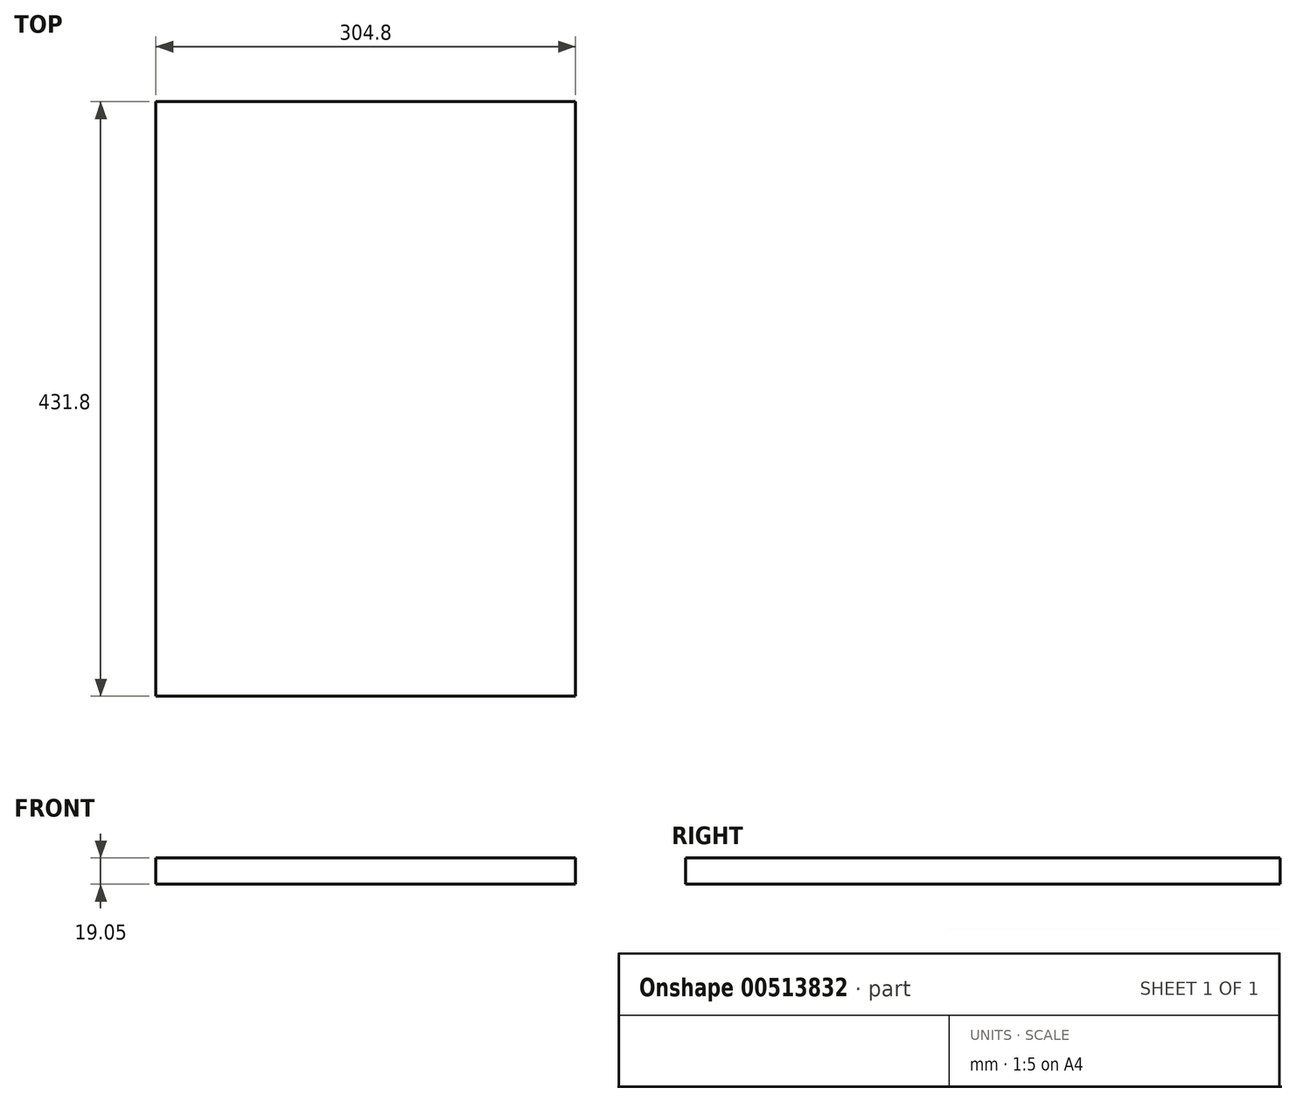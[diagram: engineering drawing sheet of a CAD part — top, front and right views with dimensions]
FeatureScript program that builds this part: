
annotation { "Feature Type Name" : "Feature", "Feature Type Description" : "" }
export const myFeature = defineFeature(function(context is Context, id is Id, definition is map)
    precondition{}
    {
        {
            var Q0;
            Q0=qCreatedBy(makeId("Top.planeOp"),FACE);
            var sketch = newSketch(context, id + "F0", { "sketchPlane" : qUnion([Q0])});
            skLineSegment(sketch, "E0.bottom", {"start": v(152.4, 215.9) * mm, "end": v(-152.4, 215.9) * mm});
            skLineSegment(sketch, "E0.top", {"start": v(152.4, -215.9) * mm, "end": v(-152.4, -215.9) * mm});
            skLineSegment(sketch, "E0.left", {"start": v(152.4, 215.9) * mm, "end": v(152.4, -215.9) * mm});
            skLineSegment(sketch, "E0.right", {"start": v(-152.4, 215.9) * mm, "end": v(-152.4, -215.9) * mm});
            skPoint(sketch, "E0.middle", {"position": v(0, 0) * mm});
            skSolve(sketch);
        }
        {
            var Q0;
            Q0 = qSketchRegion(id + "F0", true);
            extrude(context, id + "F1", {"entities" : qUnion([Q0]), "depth" : 19.05 * mm});
        }
    });
